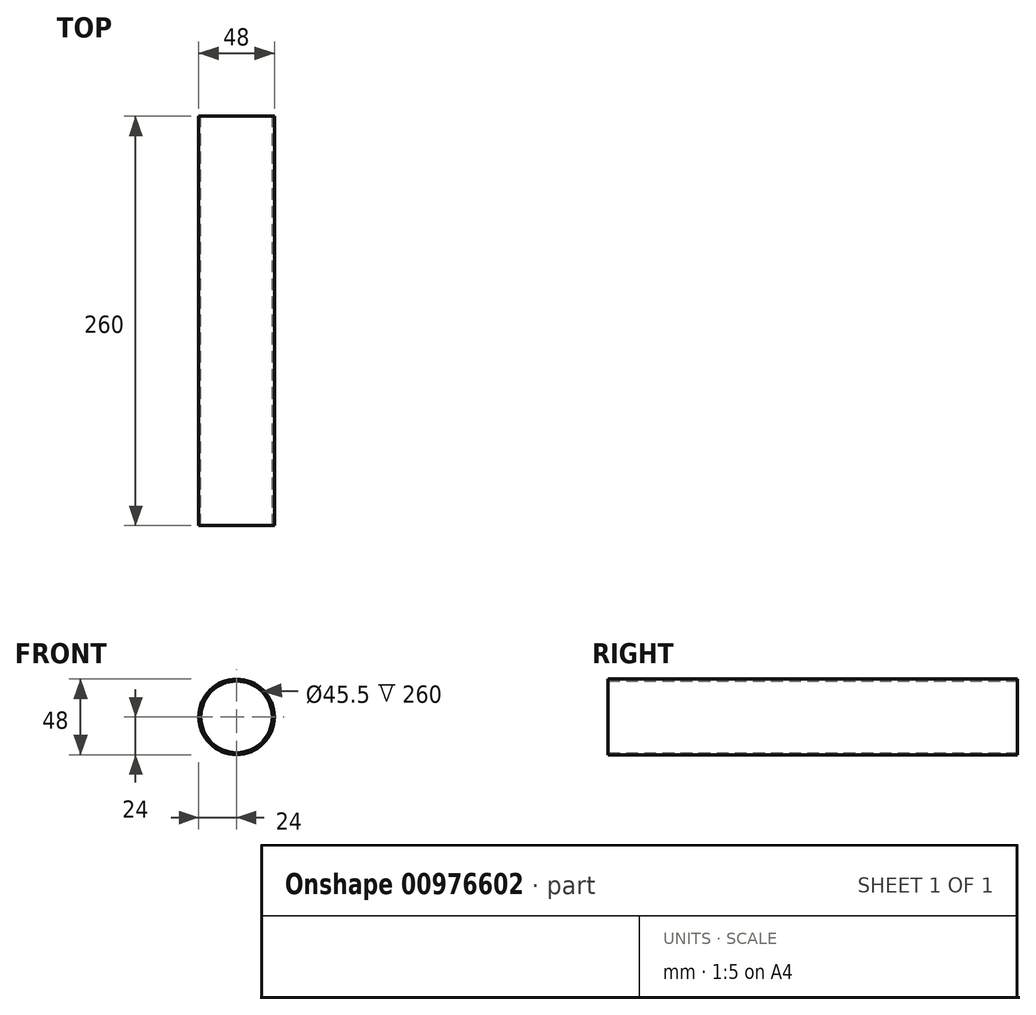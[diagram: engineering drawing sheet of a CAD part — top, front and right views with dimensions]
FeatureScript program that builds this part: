
annotation { "Feature Type Name" : "Feature", "Feature Type Description" : "" }
export const myFeature = defineFeature(function(context is Context, id is Id, definition is map)
    precondition{}
    {
        {
            var Q0;
            Q0=qCreatedBy(makeId("Front.planeOp"),FACE);
            var sketch = newSketch(context, id + "F0", { "sketchPlane" : qUnion([Q0])});
            skCircle(sketch, "E0", {"center": v(0, 0) * mm, "radius": 24 * mm});
            skCircle(sketch, "E1", {"center": v(0, 0) * mm, "radius": 22.75 * mm});
            skSolve(sketch);
        }
        {
            var Q0;
            Q0=makeQuery(id+"F0.imprint","IMPRINT",FACE,{"disambiguationData":[TD([[makeQuery(id+"F0.imprint","IMPRINT",EDGE,{"derivedFrom":sQuery(id+"F0.wireOp",EDGE,"E0")}),1.0]])]});
            extrude(context, id + "F1", {"entities" : qUnion([Q0]), "depth" : 260 * mm, "offsetDistance" : 25 * mm, "symmetric" : true});
        }
    });
